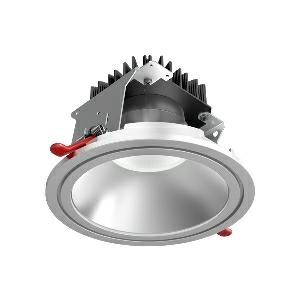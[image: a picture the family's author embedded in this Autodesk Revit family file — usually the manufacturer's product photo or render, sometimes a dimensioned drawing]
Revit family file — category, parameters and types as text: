
# Revit family: dotoo_spot_-_dse_1000_830_d_00806082_b500
name_source: partatom
category: Lighting Fixtures
units: mm (PartAtom-declared; Revit-internal decimal feet)

## family parameters
Cut with Voids When Loaded = No
Host = Face
Light Source = No
Part Type = Normal
Room Calculation Point = No
Round Connector Dimension = Use Diameter
Shared = No

## types (1)
- DOTOO.spot - DSE 1000/830/D (1 x LED, 1400 lm, 3000K)
    Apparent Load = 14 VA
    Approval mark = CE
    CIE Flux Codes = 87 99 100 100 100
    Color Rendering = 80-89
    Color Temperature = 3000K
    Control Gear = Electronic ballast
    Default Elevation = 1800 mm
    Description = DSE 1000/830/D|Recessed luminaire|light source: LED|work equipment: Electronic ballast|connected load: 220-240V, 50/60Hz|Power consumption: approx. 14 W|standby: approx. 0,20|power factor: approx. 0,900|luminous flux: 1400 lm|luminous efficacy: 100 lm/W|light distribution: Direct|direct ratio: approx. 100 %|colour temperature: Warm white, ca. 3000 K|color rendering index (CRI): >= 80|chromaticity tolerance:  3 SDCM|System of protection: IP 20|class of protection: II|technology: Continuously dimmable|operation: External|luminaire body|material: Sheet metal|colour: White|weight (net): approx. 0.7 kg|mains lead: 0.35 m Connector|Fastening: Tension spring|glare control: Prism aperture|luminance(L65): <= 2100 cd/m|unified glare rating(4H 8H): <=  19|special features: TouchDIM - dimming via standard switch, Integration into DALI light management systems, Flicker-free, Low installation depth thanks to external ballast, Suitable as emergency lighting, Ceiling installation without tools by means of tension springs, Strain relief with the possibility of through-wiring, As supplement for room depths and walking areas|
    Height = 0 mm  [stored 0 ft]
    Lamp = 1 x LED
    Lamp Light Flux = 1400 lm
    Lamp count = 1
    Length = 166 mm
    Luminous efficacy = 100 lm/W
    Manufacturer = Waldmann
    ModVariant = No
    Model = 00806082
    Mounting Place = Ceiling
    Mounting Type = Recessed
    Number of Poles = 1
    OnlyDefault = Yes
    Power Factor = 1
    Product Name = DOTOO.spot - DSE 1000/830/D
    Product group = Recessed luminaire
    ProductGroupID = 4
    Protection Class = Protection class II
    Protection Degree = IP 20
    RLX_Detail_Level = 1
    RLX_Emergency_Light_Flux = 0 lm
    RLX_Emergency_Type = 0
    RLX_Emergency_Type_DB = No
    RlxData = <blob elided: 54289 chars, md5=624649b8>
    Socket = socket
    Standby Power = 0 W
    System Light Flux = 1400 lm
    System Power = 14 W
    Type Comments = Product without accessories
    Type Image = 114272000-00806084.jpg
    URL = http://relux.com
    VarID = ---
    Voltage = 230 V
    Voltage Range = 220-240 V
    Weight = 0.00 kg
    Width = 0 mm  [stored 0 ft]

note: [stored X ft] marks values corroborated as IEEE doubles in the binary element streams (Revit-internal decimal feet)

## geometry (parser evidence)
native form markers: Blend x4, Sweep x10
no freeform markers — native parametric forms only
